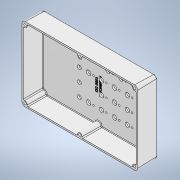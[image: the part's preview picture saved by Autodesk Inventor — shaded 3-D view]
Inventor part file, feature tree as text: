
AUTODESK INVENTOR PART (.ipt)
format: ipt  version: 2022.2 (Build 262287000, 287)  size: 675,328 bytes
history: native  units: in
note: dims shown in document units (in); Inventor stores cm internally (conversion verified against a paired STEP export)
features: extrude x1, sketch x1
ambient origin geometry x8: Origin, YZ Plane, XZ Plane, XY Plane, X Axis, Y Axis, Z Axis, Center Point
bodies: Solid2 (feature_tree), Solid1 (feature_tree)
feature tree (2):
  extrude  "Extrusion1"  Depth=0.3937in
  sketch  "Sketch1"  dims[d8=0.254in d9=0.2913in d10=0.27in d11=0.65in d12=0.7874in d13=0.7874in d14=1.5748in d16=0.8268in d17=0.3937in d19=0.3937in d21=0.5in d22=0.375in d23=0.2913in d24=0.7874in d25=1.9685in d27=0.8268in d28=0.3937in d30=0.3937in d33=0.0394in d34=0.2913in d35=0.7874in d36=1.5748in d38=0.8268in d39=0.3937in d41=0.3937in d43=0.5906in d44=0.7874in d46=1.6535in d47=0.3937in d49=0.3937in d51=0.5906in d52=0.254in d53=0.8268in d54=0.5906in d55=1.5748in d56=0.3937in d57=0.0in d58=0.3071in d59=0.113in d60=1.5748in d62=0.8268in d63=0.3937in d65=0.3937in d67=1.9685in d69=0.8268in d70=1.1811in d72=0.8268in d75=0.3071in d76=0.8268in]
